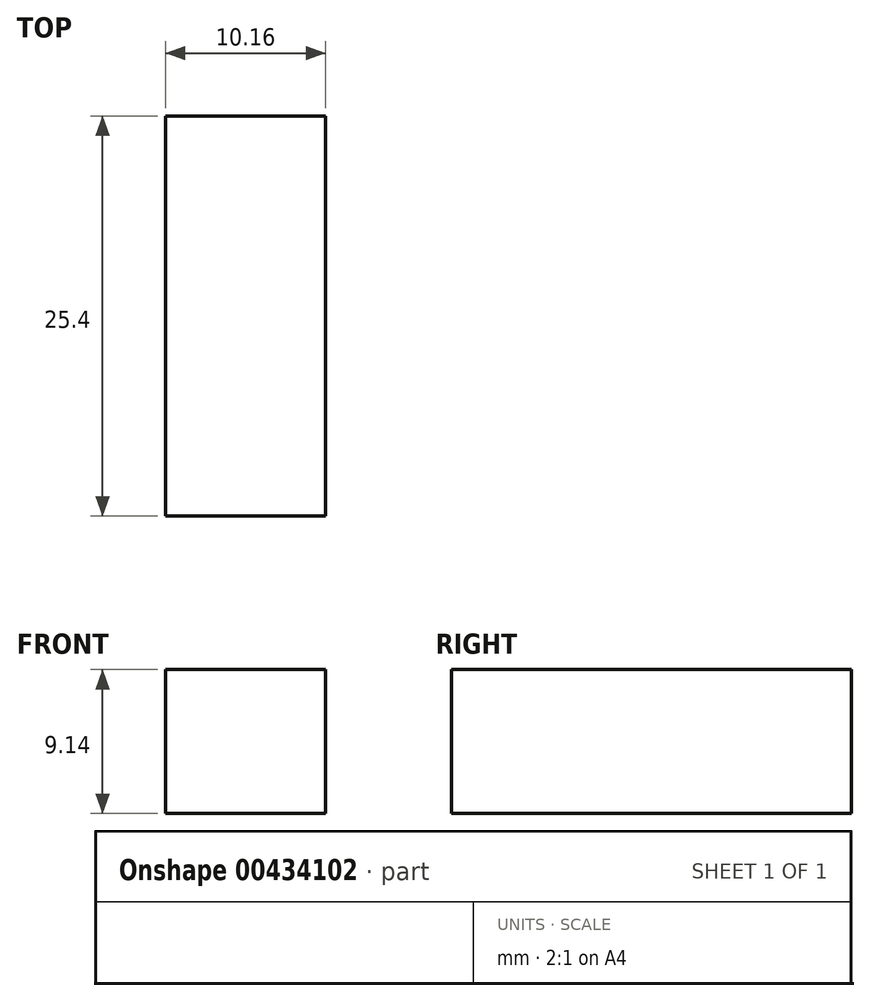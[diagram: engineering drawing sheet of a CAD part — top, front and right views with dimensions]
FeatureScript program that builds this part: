
annotation { "Feature Type Name" : "Feature", "Feature Type Description" : "" }
export const myFeature = defineFeature(function(context is Context, id is Id, definition is map)
    precondition{}
    {
        {
            var Q0;
            Q0=qCreatedBy(makeId("Top.planeOp"),FACE);
            var sketch = newSketch(context, id + "F0", { "sketchPlane" : qUnion([Q0])});
            skLineSegment(sketch, "E0.bottom", {"start": v(-5.08, 12.7) * mm, "end": v(5.08, 12.7) * mm});
            skLineSegment(sketch, "E0.top", {"start": v(-5.08, -12.7) * mm, "end": v(5.08, -12.7) * mm});
            skLineSegment(sketch, "E0.left", {"start": v(-5.08, 12.7) * mm, "end": v(-5.08, -12.7) * mm});
            skLineSegment(sketch, "E0.right", {"start": v(5.08, 12.7) * mm, "end": v(5.08, -12.7) * mm});
            skSolve(sketch);
        }
        {
            var Q0;
            Q0=makeQuery(id+"F0.imprint","IMPRINT",FACE,{"disambiguationData":[TD([[makeQuery(id+"F0.imprint","IMPRINT",EDGE,{"derivedFrom":sQuery(id+"F0.wireOp",EDGE,"E0.bottom")}),-1.0]])]});
            extrude(context, id + "F1", {"entities" : qUnion([Q0]), "depth" : 9.14 * mm});
        }
    });
